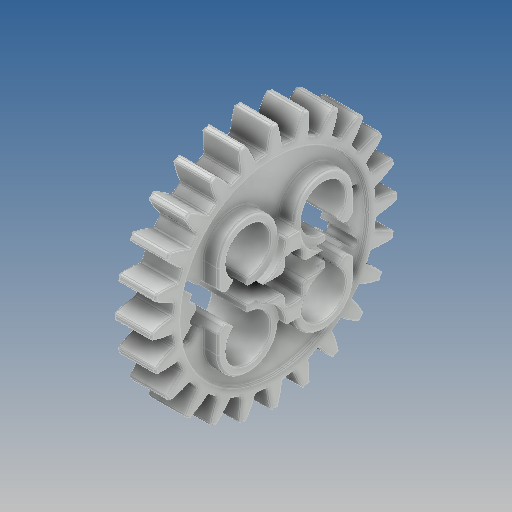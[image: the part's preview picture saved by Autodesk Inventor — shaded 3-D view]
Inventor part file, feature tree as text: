
AUTODESK INVENTOR PART (.ipt)
format: ipt  version: 2020 (Build 240168000, 168)  size: 1,725,440 bytes
history: mixed  units: mm
features: fillet x1, imported_body x1
ambient origin geometry x8: Origin, YZ Plane, XZ Plane, XY Plane, X Axis, Y Axis, Z Axis, Center Point
bodies: Solid1 (imported_parasolid)
feature tree (2):
  fillet  "Redondeo6"  [1 undecoded]
  imported_body  NMx_Import_Brep_tag  [imported B-rep: ~83 faces, bbox_mm=[4.0, 11.614208, 9.968773]]
note: 1 required parameter value undecoded (feature->parameter linkage not recoverable at this tier; creation-order binding heuristic only, values carry confidence <= 0.55)
